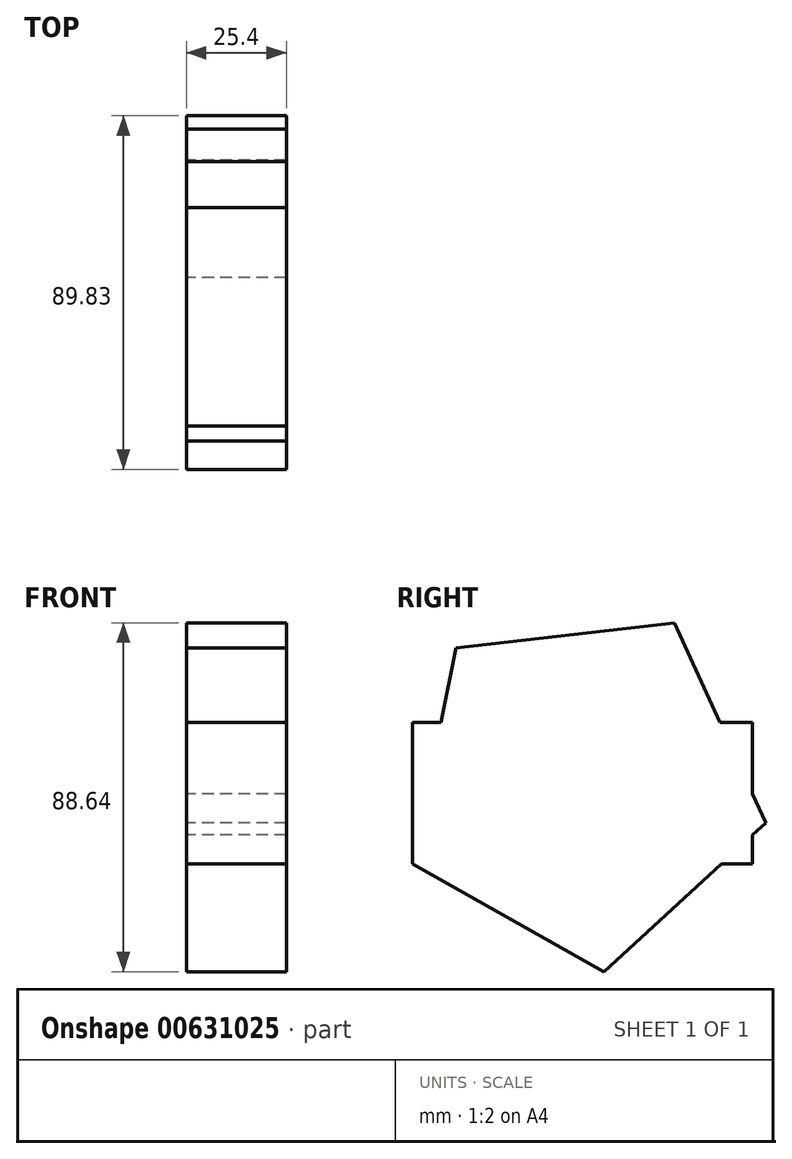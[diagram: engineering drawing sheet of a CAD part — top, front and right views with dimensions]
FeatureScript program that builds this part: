
annotation { "Feature Type Name" : "Feature", "Feature Type Description" : "" }
export const myFeature = defineFeature(function(context is Context, id is Id, definition is map)
    precondition{}
    {
        {
            var Q0;
            Q0=qCreatedBy(makeId("Right.planeOp"),FACE);
            var sketch = newSketch(context, id + "F0", { "sketchPlane" : qUnion([Q0])});
            skLineSegment(sketch, "E0.bottom", {"start": v(-30.94, 47.11) * mm, "end": v(55.51, 47.11) * mm});
            skLineSegment(sketch, "E0.top", {"start": v(-30.94, 11.21) * mm, "end": v(55.51, 11.21) * mm});
            skLineSegment(sketch, "E0.left", {"start": v(-30.94, 47.11) * mm, "end": v(-30.94, 11.21) * mm});
            skLineSegment(sketch, "E0.right", {"start": v(55.51, 47.11) * mm, "end": v(55.51, 11.21) * mm});
            skCircle(sketch, "E1.cCircle", {"center": v(12.29, 31) * mm, "radius": 47.54 * mm, "construction": true});
            skPoint(sketch, "E1.cCircle.centerSnap0", {"position": v(12.29, 47.11) * mm});
            skLineSegment(sketch, "E1.0", {"start": v(-30.94, 11.21) * mm, "end": v(-19.88, 66) * mm});
            skLineSegment(sketch, "E1.1", {"start": v(-19.88, 66) * mm, "end": v(35.63, 72.4) * mm});
            skLineSegment(sketch, "E1.2", {"start": v(35.63, 72.4) * mm, "end": v(58.89, 21.6) * mm});
            skLineSegment(sketch, "E1.3", {"start": v(58.89, 21.6) * mm, "end": v(17.75, -16.23) * mm});
            skLineSegment(sketch, "E1.4", {"start": v(17.75, -16.23) * mm, "end": v(-30.94, 11.21) * mm});
            skSolve(sketch);
        }
        {
            var Q0;
            Q0 = qSketchRegion(id + "F0", true);
            extrude(context, id + "F1", {"entities" : qUnion([Q0]), "depth" : 25.4 * mm, "offsetDistance" : 25.4 * mm});
        }
    });
